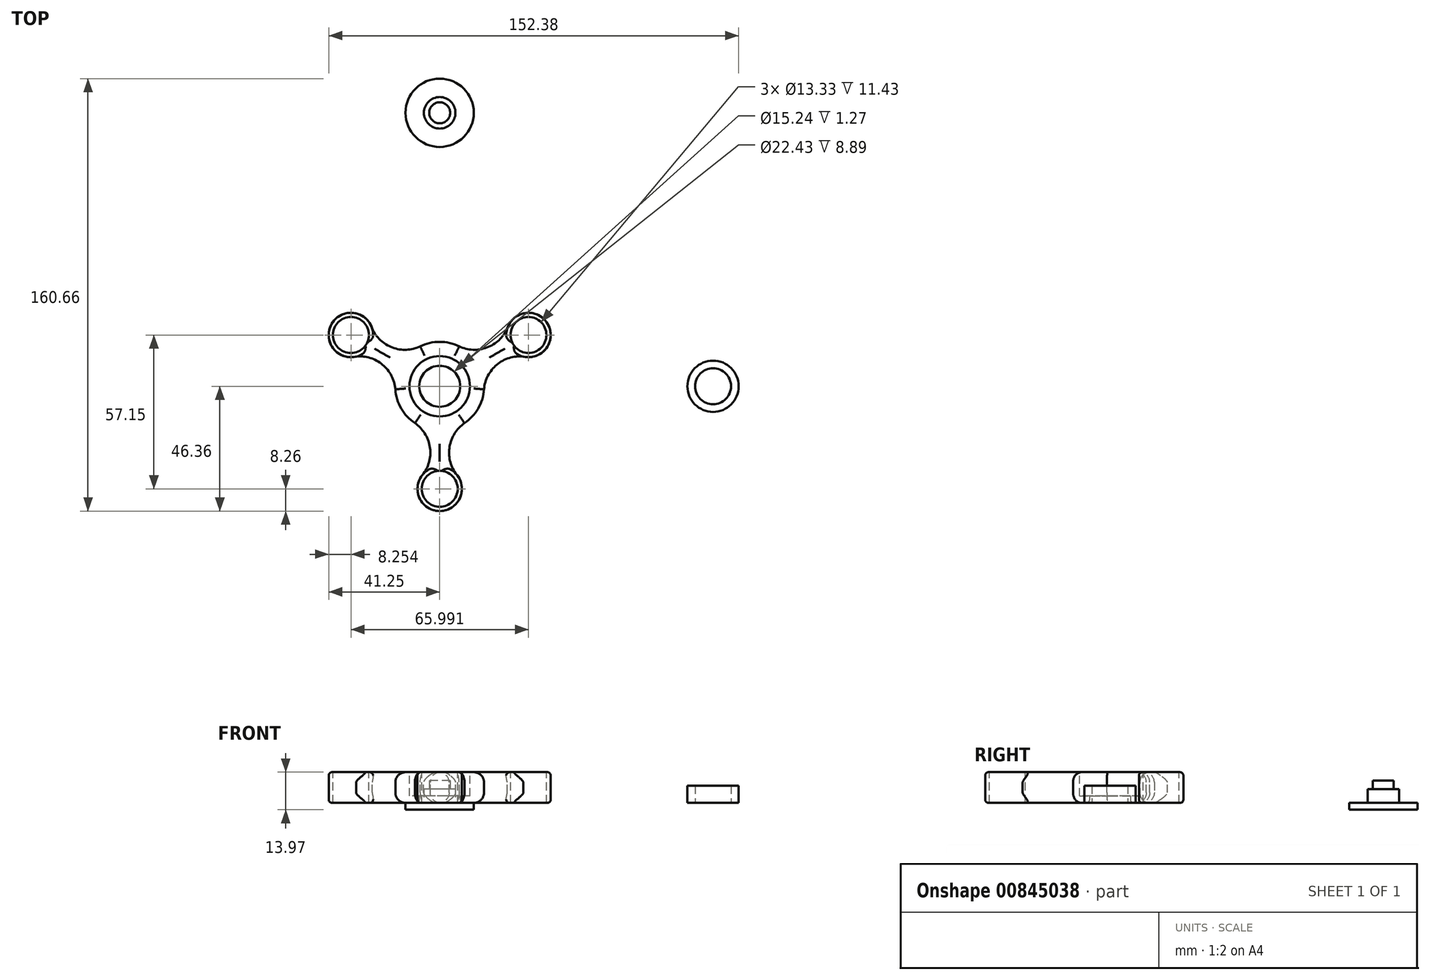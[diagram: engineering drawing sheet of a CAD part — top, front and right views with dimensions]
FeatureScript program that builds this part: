
annotation { "Feature Type Name" : "Feature", "Feature Type Description" : "" }
export const myFeature = defineFeature(function(context is Context, id is Id, definition is map)
    precondition{}
    {
        {
            var Q0;
            Q0=qCreatedBy(makeId("Top.planeOp"),FACE);
            var sketch = newSketch(context, id + "F0", { "sketchPlane" : qUnion([Q0])});
            skCircle(sketch, "E0", {"center": v(0, 101.6) * mm, "radius": 5.85 * mm});
            skSolve(sketch);
        }
        {
            var Q0;
            Q0 = qSketchRegion(id + "F0", true);
            extrude(context, id + "F1", {"entities" : qUnion([Q0]), "depth" : 5.08 * mm, "offsetDistance" : 25.4 * mm});
        }
        {
            var Q0;
            Q0=makeQuery(id+"F1.opExtrude","CAP_FACE",FACE,{"disambiguationData":[OSD([sQuery(id+"F0.wireOp",EDGE,"E0")])],"isStart":false});
            var sketch = newSketch(context, id + "F2", { "sketchPlane" : qUnion([Q0])});
            skCircle(sketch, "E1", {"center": v(0, 101.6) * mm, "radius": 3.9 * mm});
            skSolve(sketch);
        }
        {
            var Q0;
            Q0 = qSketchRegion(id + "F2", true);
            extrude(context, id + "F3", {"entities" : qUnion([Q0]), "operationType" : NewBodyOperationType.ADD, "depth" : 3.17 * mm, "offsetDistance" : 25.4 * mm});
        }
        {
            var Q0;
            Q0=makeQuery(id+"F1.opExtrude","CAP_FACE",FACE,{"disambiguationData":[OSD([sQuery(id+"F0.wireOp",EDGE,"E0")])],"isStart":true});
            var sketch = newSketch(context, id + "F4", { "sketchPlane" : qUnion([Q0])});
            skCircle(sketch, "E2", {"center": v(0, -101.6) * mm, "radius": 12.7 * mm});
            skSolve(sketch);
        }
        {
            var Q0;
            Q0 = qSketchRegion(id + "F4", true);
            extrude(context, id + "F5", {"entities" : qUnion([Q0]), "operationType" : NewBodyOperationType.ADD, "depth" : 2.54 * mm, "offsetDistance" : 25.4 * mm});
        }
        {
            var Q0;
            Q0=qCreatedBy(makeId("Top.planeOp"),FACE);
            var sketch = newSketch(context, id + "F6", { "sketchPlane" : qUnion([Q0])});
            skCircle(sketch, "E3", {"center": v(101.6, 0) * mm, "radius": 9.53 * mm});
            skCircle(sketch, "E4", {"center": v(101.6, 0) * mm, "radius": 6.67 * mm});
            skSolve(sketch);
        }
        {
            var Q0;
            Q0 = qSketchRegion(id + "F6", true);
            extrude(context, id + "F7", {"entities" : qUnion([Q0]), "depth" : 6.35 * mm, "offsetDistance" : 25.4 * mm});
        }
        {
            var Q0;
            Q0=qCreatedBy(makeId("Top.planeOp"),FACE);
            var sketch = newSketch(context, id + "F8", { "sketchPlane" : qUnion([Q0])});
            skCircle(sketch, "E5", {"center": v(0, 0) * mm, "radius": 16.51 * mm});
            skCircle(sketch, "E6", {"center": v(0, 0) * mm, "radius": 7.62 * mm});
            skSolve(sketch);
        }
        {
            var Q0;
            Q0 = qSketchRegion(id + "F8", true);
            extrude(context, id + "F9", {"entities" : qUnion([Q0]), "depth" : 11.43 * mm, "offsetDistance" : 25.4 * mm});
        }
        {
            var Q0;
            Q0=makeQuery(id+"F9.opExtrude","CAP_FACE",FACE,{"disambiguationData":[OSD([sQuery(id+"F8.wireOp",EDGE,"E5"),sQuery(id+"F8.wireOp",EDGE,"E6")])],"isStart":false});
            var sketch = newSketch(context, id + "F10", { "sketchPlane" : qUnion([Q0])});
            skCircle(sketch, "E7", {"center": v(0, 0) * mm, "radius": 11.21 * mm});
            skSolve(sketch);
        }
        {
            var Q0;
            Q0 = qSketchRegion(id + "F10", true);
            extrude(context, id + "F11", {"entities" : qUnion([Q0]), "operationType" : NewBodyOperationType.REMOVE, "oppositeDirection" : true, "depth" : 8.9 * mm, "offsetDistance" : 25.4 * mm});
        }
        {
            var Q0;
            Q0=makeQuery(id+"F9.opExtrude","CAP_FACE",FACE,{"disambiguationData":[OSD([sQuery(id+"F8.wireOp",EDGE,"E5"),sQuery(id+"F8.wireOp",EDGE,"E6")])],"isStart":false});
            var sketch = newSketch(context, id + "F12", { "sketchPlane" : qUnion([Q0])});
            skArc(sketch, "E8", {"start": v(-5.99, -32.41) * mm, "mid": v(0, -46.36) * mm, "end": v(5.99, -32.41) * mm});
            skCircle(sketch, "E9", {"center": v(0, -38.1) * mm, "radius": 6.67 * mm});
            skLineSegment(sketch, "E10", {"start": v(0, -38.1) * mm, "end": v(0, 0) * mm, "construction": true});
            skLineSegment(sketch, "E11", {"start": v(9.21, -13.7) * mm, "end": v(-9.21, -13.7) * mm});
            skArc(sketch, "E12.1.0", {"start": v(31.06, 11.02) * mm, "mid": v(40.14, 23.18) * mm, "end": v(25.08, 21.4) * mm});
            skCircle(sketch, "E12.1.1", {"center": v(33, 19.05) * mm, "radius": 6.67 * mm});
            skArc(sketch, "E12.2.0", {"start": v(-25.08, 21.4) * mm, "mid": v(-40.14, 23.18) * mm, "end": v(-31.06, 11.02) * mm});
            skCircle(sketch, "E12.2.1", {"center": v(-33, 19.05) * mm, "radius": 6.67 * mm});
            skPoint(sketch, "E12.center", {"position": v(0, 0) * mm});
            skLineSegment(sketch, "E13.1.0", {"start": v(7.26, 14.83) * mm, "end": v(16.47, -1.13) * mm});
            skLineSegment(sketch, "E13.2.0", {"start": v(-16.47, -1.13) * mm, "end": v(-7.26, 14.83) * mm});
            skArc(sketch, "E14", {"start": v(9.21, -13.7) * mm, "mid": v(3.68, -22.38) * mm, "end": v(5.99, -32.41) * mm});
            skArc(sketch, "E15.MirrorCS", {"start": v(-9.21, -13.7) * mm, "mid": v(-3.68, -22.38) * mm, "end": v(-5.99, -32.41) * mm});
            skArc(sketch, "E16.1.0", {"start": v(7.26, 14.83) * mm, "mid": v(17.54, 14.38) * mm, "end": v(25.08, 21.4) * mm});
            skArc(sketch, "E16.1.1", {"start": v(16.47, -1.13) * mm, "mid": v(21.22, 8) * mm, "end": v(31.06, 11.02) * mm});
            skArc(sketch, "E16.2.0", {"start": v(-16.47, -1.13) * mm, "mid": v(-21.22, 8) * mm, "end": v(-31.06, 11.02) * mm});
            skArc(sketch, "E16.2.1", {"start": v(-7.26, 14.83) * mm, "mid": v(-17.54, 14.38) * mm, "end": v(-25.08, 21.4) * mm});
            skSolve(sketch);
        }
        {
            var Q0;
            Q0 = qSketchRegion(id + "F12", true);
            extrude(context, id + "F13", {"entities" : qUnion([Q0]), "operationType" : NewBodyOperationType.ADD, "oppositeDirection" : true, "depth" : 11.43 * mm, "offsetDistance" : 25.4 * mm});
        }
        {
            var Q0;
            Q0=makeQuery(id+"F13.opExtrude","CAP_EDGE",EDGE,{"disambiguationData":[OSD([sQuery(id+"F12.wireOp",EDGE,"E14")])],"isStart":true});
            var Q1;
            {var subQ1=sQuery(id+"F12.wireOp",EDGE,"E14");var subQ2=sQuery(id+"F8.wireOp",EDGE,"E5");Q1=makeQuery(id+"F13.boolean.opBoolean","SPLIT",EDGE,{"disambiguationData":[TD([makeQuery(id+"F13.opExtrude","SWEPT_FACE",FACE,{"disambiguationData":[OSD([subQ1])]})])],"derivedFrom":makeQuery(id+"F9.opExtrude","CAP_EDGE",EDGE,{"disambiguationData":[OSD([subQ2])],"isStart":false})});}
            var Q2;
            Q2=makeQuery(id+"F13.opExtrude","CAP_EDGE",EDGE,{"disambiguationData":[OSD([sQuery(id+"F12.wireOp",EDGE,"E15.MirrorCS")])],"isStart":true});
            var Q3;
            {var subQ0=sQuery(id+"F12.wireOp",EDGE,"E15.MirrorCS");var subQ1=sQuery(id+"F8.wireOp",EDGE,"E5");Q3=makeQuery(id+"F13.boolean.opBoolean","SPLIT",EDGE,{"disambiguationData":[TD([makeQuery(id+"F13.opExtrude","SWEPT_FACE",FACE,{"disambiguationData":[OSD([subQ0])]})])],"derivedFrom":makeQuery(id+"F9.opExtrude","CAP_EDGE",EDGE,{"disambiguationData":[OSD([subQ1])],"isStart":false})});}
            var Q4;
            Q4=makeQuery(id+"F13.opExtrude","CAP_EDGE",EDGE,{"disambiguationData":[OSD([sQuery(id+"F12.wireOp",EDGE,"E16.2.1")])],"isStart":true});
            var Q5;
            {var subQ0=sQuery(id+"F12.wireOp",EDGE,"E16.1.0");var subQ1=sQuery(id+"F8.wireOp",EDGE,"E5");Q5=makeQuery(id+"F13.boolean.opBoolean","SPLIT",EDGE,{"disambiguationData":[TD([makeQuery(id+"F13.opExtrude","SWEPT_FACE",FACE,{"disambiguationData":[OSD([subQ0])]})])],"derivedFrom":makeQuery(id+"F9.opExtrude","CAP_EDGE",EDGE,{"disambiguationData":[OSD([subQ1])],"isStart":false})});}
            var Q6;
            Q6=makeQuery(id+"F13.opExtrude","CAP_EDGE",EDGE,{"disambiguationData":[OSD([sQuery(id+"F12.wireOp",EDGE,"E16.1.0")])],"isStart":false});
            var Q7;
            {var subQ0=sQuery(id+"F12.wireOp",EDGE,"E16.1.0");var subQ1=sQuery(id+"F8.wireOp",EDGE,"E5");Q7=makeQuery(id+"F13.boolean.opBoolean","SPLIT",EDGE,{"disambiguationData":[TD([makeQuery(id+"F13.opExtrude","SWEPT_FACE",FACE,{"disambiguationData":[OSD([subQ0])]})])],"derivedFrom":makeQuery(id+"F9.opExtrude","CAP_EDGE",EDGE,{"disambiguationData":[OSD([subQ1])],"isStart":true})});}
            var Q8;
            {var subQ1=sQuery(id+"F12.wireOp",EDGE,"E14");var subQ2=sQuery(id+"F8.wireOp",EDGE,"E5");Q8=makeQuery(id+"F13.boolean.opBoolean","SPLIT",EDGE,{"disambiguationData":[TD([makeQuery(id+"F13.opExtrude","SWEPT_FACE",FACE,{"disambiguationData":[OSD([subQ1])]})])],"derivedFrom":makeQuery(id+"F9.opExtrude","CAP_EDGE",EDGE,{"disambiguationData":[OSD([subQ2])],"isStart":true})});}
            var Q9;
            {var subQ0=sQuery(id+"F12.wireOp",EDGE,"E15.MirrorCS");var subQ1=sQuery(id+"F8.wireOp",EDGE,"E5");Q9=makeQuery(id+"F13.boolean.opBoolean","SPLIT",EDGE,{"disambiguationData":[TD([makeQuery(id+"F13.opExtrude","SWEPT_FACE",FACE,{"disambiguationData":[OSD([subQ0])]})])],"derivedFrom":makeQuery(id+"F9.opExtrude","CAP_EDGE",EDGE,{"disambiguationData":[OSD([subQ1])],"isStart":true})});}
            fillet(context, id + "F14", {"entities" : qUnion([Q0, Q1, Q2, Q3, Q4, Q5, Q6, Q7, Q8, Q9]), "radius" : 3.8 * mm, "tangentPropagation" : true, "allowEdgeOverflow" : false});
        }
        {
            var Q0;
            Q0=makeQuery(id+"F13.opExtrude","CAP_EDGE",EDGE,{"disambiguationData":[OSD([sQuery(id+"F12.wireOp",EDGE,"E12.2.0")])],"isStart":true});
            var Q1;
            Q1=makeQuery(id+"F13.opExtrude","CAP_EDGE",EDGE,{"disambiguationData":[OSD([sQuery(id+"F12.wireOp",EDGE,"E12.2.0")])],"isStart":false});
            var Q2;
            Q2=makeQuery(id+"F13.opExtrude","CAP_EDGE",EDGE,{"disambiguationData":[OSD([sQuery(id+"F12.wireOp",EDGE,"E8")])],"isStart":false});
            var Q3;
            Q3=makeQuery(id+"F13.opExtrude","CAP_EDGE",EDGE,{"disambiguationData":[OSD([sQuery(id+"F12.wireOp",EDGE,"E12.1.0")])],"isStart":false});
            var Q4;
            Q4=makeQuery(id+"F13.opExtrude","CAP_EDGE",EDGE,{"disambiguationData":[OSD([sQuery(id+"F12.wireOp",EDGE,"E12.1.0")])],"isStart":true});
            var Q5;
            Q5=makeQuery(id+"F13.opExtrude","CAP_EDGE",EDGE,{"disambiguationData":[OSD([sQuery(id+"F12.wireOp",EDGE,"E8")])],"isStart":true});
            var Q6;
            Q6=makeQuery(id+"F11.boolean.opBoolean","COPY",EDGE,{"derivedFrom":makeQuery(id+"F11.opExtrude","CAP_EDGE",EDGE,{"disambiguationData":[OSD([sQuery(id+"F10.wireOp",EDGE,"E7")])],"isStart":true})});
            var Q7;
            Q7=makeQuery(id+"F9.opExtrude","CAP_EDGE",EDGE,{"disambiguationData":[OSD([sQuery(id+"F8.wireOp",EDGE,"E6")])],"isStart":true});
            fillet(context, id + "F15", {"entities" : qUnion([Q0, Q1, Q2, Q3, Q4, Q5, Q6, Q7]), "radius" : 1.27 * mm, "tangentPropagation" : true, "allowEdgeOverflow" : false});
        }
    });
